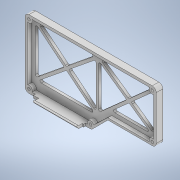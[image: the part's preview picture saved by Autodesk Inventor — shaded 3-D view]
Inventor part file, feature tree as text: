
AUTODESK INVENTOR PART (.ipt)
format: ipt  version: 2021 (Build 250183000, 183)  size: 531,968 bytes
history: native  units: mm
features: sketch x22, extrude x20, fillet x5, hole x2, chamfer x2
ambient origin geometry x8: Origin, YZ Plane, XZ Plane, XY Plane, X Axis, Y Axis, Z Axis, Center Point
bodies: Solid1 (feature_tree)
feature tree (51):
  extrude  "Extrusion1"  Depth=100.0mm
  extrude  "Extrusion2"  Depth=50.0mm
  hole  "Hole1"  [1 undecoded]
  extrude  "Extrusion3"  Depth=50.0mm
  extrude  "Extrusion4"  Depth=3.0mm
  extrude  "Extrusion5"  Depth=3.0mm
  fillet  "Fillet1"  Radius=49.0mm
  extrude  "Extrusion6"  Depth=49.0mm
  extrude  "Extrusion7"  Depth=5.0mm
  extrude  "Extrusion8"  Depth=5.0mm
  chamfer  "Chamfer1"  Distance=3.0mm
  extrude  "Extrusion9"  Depth=12.5mm
  fillet  "Fillet2"  Radius=63.1mm
  extrude  "Extrusion11"  Depth=3.0mm
  extrude  "Extrusion12"  Depth=2.0mm
  chamfer  "Chamfer2"  Distance=3.0mm
  extrude  "Extrusion13"  Depth=33.2mm
  extrude  "Extrusion14"  Depth=33.2mm
  extrude  "Extrusion15"  Depth=33.2mm
  fillet  "Fillet3"  Radius=3.0mm
  fillet  "Fillet4"  Radius=5.0mm
  hole  "Hole2"  [1 undecoded]
  extrude  "Extrusion20"  Depth=12.0mm TaperAngle=0.0deg
  extrude  "Extrusion21"  Depth=33.2mm
  fillet  "Fillet5"  Radius=1.2mm
  extrude  "Extrusion22"  Depth=3.0mm
  extrude  "Extrusion23"  Depth=14.0mm
  extrude  "Extrusion24"  Depth=1.2mm
  extrude  "Extrusion25"  Depth=33.2mm
  sketch  "Sketch1"  dims[d0=52.0mm d1=100.0mm]
  sketch  "Sketch2"  dims[d2=26.0mm d3=50.0mm]
  sketch  "Sketch3"  dims[d4=2.0mm d5=0.0mm d6=3.0mm]
  sketch  "Sketch4"  dims[d7=3.0mm d8=50.0mm]
  sketch  "Sketch5"  dims[d9=3.0mm d10=97.0mm]
  sketch  "Sketch6"  dims[d11=15.0mm d12=3.0mm d13=49.0mm]
  sketch  "Sketch7"  dims[d14=97.0mm d15=49.0mm]
  sketch  "Sketch8"  dims[d16=2.0mm d17=5.0mm]
  sketch  "Sketch9"  dims[d18=2.0mm d19=5.0mm]
  sketch  "Sketch10"  dims[d20=2.0mm]
  sketch  "Sketch12"  dims[d21=5.0mm]
  sketch  "Sketch13"  dims[d22=2.0mm]
  sketch  "Sketch14"  dims[d23=5.0mm]
  sketch  "Sketch15"  dims[d24=2.0mm]
  sketch  "Sketch16"  dims[d25=5.0mm d26=3.0mm d27=0.0mm]
  sketch  "Sketch17"  dims[d28=2.0mm d29=6.0mm d30=5.0mm d31=2.0mm d32=90.0deg d33=10.0mm d34=20.594885mm d35=12.5mm d36=63.1mm]
  sketch  "Sketch23"  dims[d37=3.0mm d38=0.0mm d39=50.673mm]
  sketch  "Sketch24"  dims[d40=3.0mm d41=0.0mm d42=2.0mm]
  sketch  "Sketch25"  dims[d43=2.0mm]
  sketch  "Sketch26"  dims[d44=2.0mm]
  sketch  "Sketch27"  dims[d45=1.5mm d46=3.0mm d47=0.0mm]
  sketch  "Sketch28"  dims[d48=3.0mm d49=7.6mm d50=46.4mm d51=6.7mm d52=3.0mm d53=0.0mm d54=5.0mm d55=2.0mm d56=12.0mm d57=0.0mm d58=1.4mm d59=1.2mm d60=3.0mm d61=14.0mm d62=1.2mm d63=1.4mm d64=12.0mm d65=3.0mm d66=0.0mm d67=1.0mm d68=2.0mm d69=45.0deg d70=1.2mm d71=3.0mm d72=0.0mm d73=1.0mm d77=3.0mm d78=0.0mm d79=3.0mm d80=3.0mm d81=3.0mm d82=3.0mm d83=3.0mm d84=3.0mm d85=3.0mm d86=48.0mm d87=2.0mm d88=0.0mm d89=8.4mm d90=2.0mm d91=45.0deg d92=1.2mm d93=3.0mm d94=0.0mm d95=7.6mm d96=5.0mm d97=0.0mm d98=2.0mm d99=2.0mm d100=2.0mm d101=2.0mm d102=2.0mm d103=2.0mm d104=0.0mm d105=1.0mm d106=1.0mm d107=2.0mm d108=6.0mm d109=5.0mm d110=2.0mm d111=90.0deg d112=4.0mm d113=20.594885mm d146=6.5mm d147=5.0mm d148=2.0mm d149=0.0mm d150=0.3mm d151=0.3mm d152=2.0mm d153=0.0mm d154=3.0mm d155=2.0mm d156=2.0mm d157=2.0mm d158=2.0mm d159=0.0mm d160=1.5mm d161=2.811mm d162=12.0mm d163=33.2mm d164=2.0mm d165=0.0mm d166=2.581mm d167=8.726646mm d168=2.0mm d169=33.2mm d170=0.0mm d171=1.2mm d172=33.2mm d173=0.0mm d74=0.872665mm d75=0.872665mm d76=0.5mm d114=0.75mm d115=20.594885mm d116=0.0625mm d117=0.75mm d118=0.375mm]
note: 2 required parameter values undecoded (feature->parameter linkage not recoverable at this tier; creation-order binding heuristic only, values carry confidence <= 0.55)
